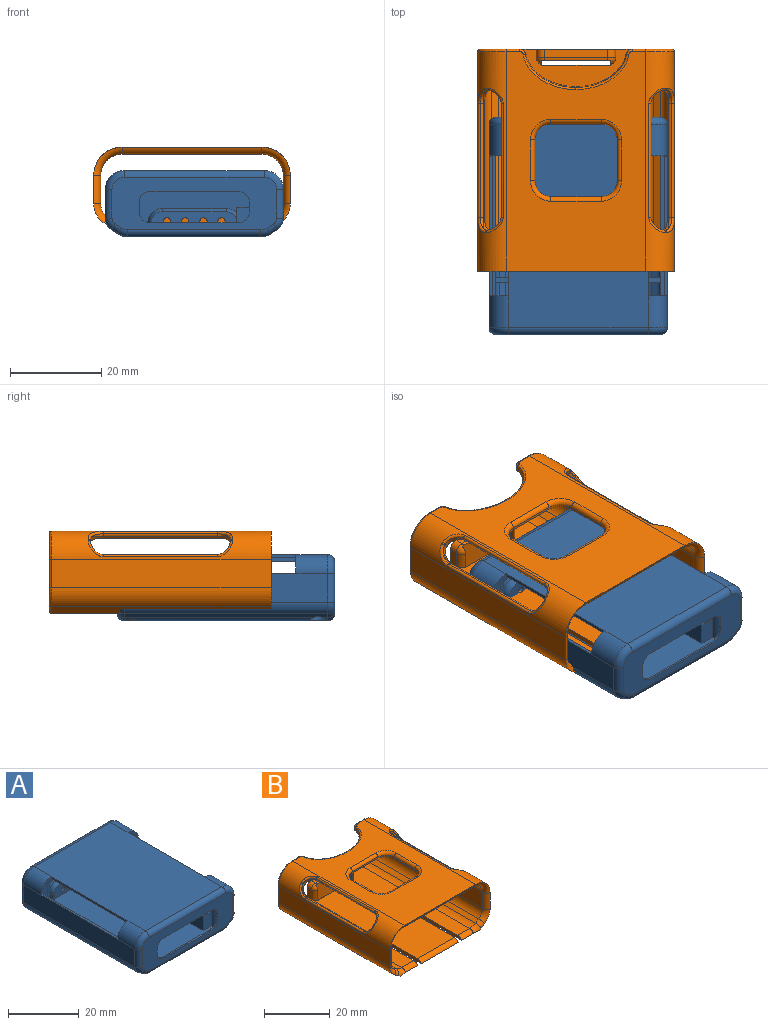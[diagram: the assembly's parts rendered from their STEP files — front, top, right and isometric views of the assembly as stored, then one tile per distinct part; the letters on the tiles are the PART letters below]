
ASSEMBLY  parts=2 mates=1
PART A: 181 faces, bbox 40.3x48.1x15.7 mm
  f0: plane 29.28x1.41mm, normal (-0.55,0,0.84), area 49.5mm2, adj f1,f15,f31,f117,f175
  f1: cylinder r=2.5mm len=29.28mm, axis (0,1,0), area 19.4mm2, adj f0,f9,f15,f31,f117
  f2: plane 5.36x1.41mm, normal (0.55,0,0.84), area 9.1mm2, adj f3,f17,f113,f178
  f3: cylinder r=2.5mm len=5.42mm, axis (0,1,0), area 7.8mm2, adj f2,f9,f17,f39,f113
  f4: plane 11.52x1.2mm, normal (1,0,0), area 12.3mm2, adj f6,f7,f9,f19,f72,f73
  f5: plane 11.52x1.2mm, normal (-1,0,0), area 12.3mm2, adj f6,f7,f8,f9,f72,f73
  f6: plane 27.05x9.99mm, normal (0,1,0), area 108.2mm2, adj f4,f5,f9,f72,f74,f75,f76,f77
  f7: plane 44.69x30.71mm, normal (0,0,-1), area 1224.5mm2, adj f4,f5,f8,f15,f16,f17,f18,f19
  f8: cylinder r=2.5mm len=11.52mm, axis (0,0,-1), area 52.4mm2, adj f5,f7,f9,f23,f32,f61,f62,f63
  f9: plane 45.69x29.18mm, normal (0,0,1), area 1231.9mm2, adj f1,f3,f4,f5,f6,f8,f15,f16
  f10: plane 30.69x0.7mm, normal (0,0,1), area 21.5mm2, adj f11,f12,f21,f54
  f11: plane 4.2x4.2mm, normal (0,1,0), area 4.2mm2, adj f10,f56,f125,f141
  f12: plane 4.2x4.2mm, normal (0,-1,0), area 4.2mm2, adj f10,f56,f123,f140
  f13: plane 44.69x6.23mm, normal (-1,0,0), area 278.4mm2, adj f46,f132,f138,f139,f144,f169
  f14: plane 35.64x6.23mm, normal (1,0,0), area 169.1mm2, adj f17,f18,f64,f66,f67,f111,f112,f113
  f15: plane 11.52x3.5mm, normal (0,-1,0), area 36.1mm2, adj f0,f1,f7,f9,f16,f22,f119,f175
  f16: cylinder r=2.5mm len=11.52mm, axis (0,0,-1), area 70.8mm2, adj f7,f9,f15,f50
  f17: plane 11.46x2.92mm, normal (0,1,0), area 29.5mm2, adj f2,f3,f7,f14,f19,f39,f120,f178
  f18: plane 11.52x3.5mm, normal (0,-1,0), area 36.1mm2, adj f7,f9,f14,f20,f27,f29,f118,f177
  f19: cylinder r=2.5mm len=11.52mm, axis (0,0,-1), area 56.4mm2, adj f4,f7,f9,f17,f39
  f20: cylinder r=2.5mm len=11.52mm, axis (0,0,-1), area 70.8mm2, adj f7,f9,f18,f50
  f21: plane 44.69x6.23mm, normal (1,0,0), area 278.4mm2, adj f10,f133,f140,f141,f147,f162
  f22: plane 35.64x6.23mm, normal (-1,0,0), area 169.1mm2, adj f15,f23,f51,f52,f53,f115,f116,f117
  f23: plane 11.46x2.92mm, normal (0,1,0), area 29.5mm2, adj f7,f8,f22,f28,f30,f32,f121,f176
  f24: plane 44.8x1.53mm, normal (-0.55,0,-0.84), area 74.9mm2, adj f102,f132,f135,f136,f148,f173
  f25: plane 45.15x1.88mm, normal (0.55,0,-0.84), area 74.9mm2, adj f84,f133,f134,f137,f151,f166
  f26: plane 44.69x29.18mm, normal (0,0,-1), area 1219.4mm2, adj f84,f90,f96,f102,f130,f131,f134,f135
  f27: plane 29.28x1.41mm, normal (0.55,0,0.84), area 49.5mm2, adj f18,f29,f112,f177
  f28: plane 5.36x1.41mm, normal (-0.55,0,0.84), area 9.1mm2, adj f23,f30,f116,f176
  f29: cylinder r=2.5mm len=29.28mm, axis (0,1,0), area 42.4mm2, adj f9,f18,f27,f112
  f30: cylinder r=2.5mm len=5.42mm, axis (0,1,0), area 7.8mm2, adj f9,f23,f28,f32,f116
  f31: cylinder r=2.5mm len=25.54mm, axis (0,1,0), area 23mm2, adj f0,f1,f117
  f32: cylinder r=2.5mm len=4.99mm, axis (0,0,-1), area 7.3mm2, adj f8,f9,f23,f30
  f33: revolved ~3.2x3.2mm, area 7.9mm2, adj f34,f37,f38,f41
  f34: cylinder r=2mm len=14mm, axis (1,0,0), area 23.7mm2, adj f33,f35,f37,f42
  f35: revolved ~3.2x3.2mm, area 7.9mm2, adj f34,f36,f37,f43
  f36: cylinder r=2mm len=1.5mm, axis (0,0,-1), area 2.5mm2, adj f9,f35,f37,f44
  f37: plane 19.05x4.03mm, normal (0,-1,0), area 65.8mm2, adj f9,f33,f34,f35,f36,f38,f106,f107
  f38: cylinder r=2mm len=1.5mm, axis (0,0,-1), area 2.5mm2, adj f9,f33,f37,f40
  f39: extruded ~4.99x2.25mm, area 13.9mm2, adj f3,f9,f17,f19
  f40: plane 1.5x0.8mm, normal (-1,0,0), area 1.2mm2, adj f9,f38,f41,f50
  f41: cylinder r=3.2mm len=3.2mm, axis (0,1,0), area 4mm2, adj f33,f40,f42,f50
  f42: plane 14x0.8mm, normal (0,0,1), area 11.2mm2, adj f34,f41,f43,f50
  f43: cylinder r=3.2mm len=3.2mm, axis (0,1,0), area 4mm2, adj f35,f42,f44,f50
  f44: plane 1.5x0.8mm, normal (1,0,0), area 1.2mm2, adj f9,f36,f43,f50
  f45: plane 36.11x11.52mm, normal (0,-1,0), area 245.6mm2, adj f74,f75,f76,f77,f128,f129,f162,f163
  f46: plane 30.69x0.7mm, normal (0,0,1), area 21.5mm2, adj f13,f47,f48,f65
  f47: plane 4.2x4.2mm, normal (0,1,0), area 4.2mm2, adj f46,f55,f124,f138
  f48: plane 4.2x4.2mm, normal (0,-1,0), area 4.2mm2, adj f46,f55,f122,f139
  f49: plane 36.11x11.52mm, normal (0,1,0), area 307.5mm2, adj f142,f143,f144,f145,f146,f147,f148,f149
  f50: plane 25.96x11.52mm, normal (0,-1,0), area 207.6mm2, adj f7,f9,f16,f20,f40,f41,f42,f43
  f51: plane 5x5mm, normal (0,1,0), area 6.3mm2, adj f7,f22,f52,f54,f70,f71,f121,f125
  f52: plane 33.68x0.8mm, normal (0,0,1), area 26.9mm2, adj f22,f51,f53,f54
  f53: plane 5x5mm, normal (0,-1,0), area 6.3mm2, adj f7,f22,f52,f54,f70,f71,f119,f123
  f54: plane 33.68x1.5mm, normal (-1,0,0), area 50.5mm2, adj f10,f51,f52,f53,f123,f125
  f55: plane 30.69x0.7mm, normal (-1,0,0), area 21.5mm2, adj f47,f48,f57,f68
  f56: plane 30.69x0.7mm, normal (1,0,0), area 21.5mm2, adj f11,f12,f57,f70
  f57: plane 44.69x30.71mm, normal (0,0,1), area 1372.1mm2, adj f55,f56,f138,f139,f140,f141,f143,f165
  f58: plane 11.15x4.99mm, normal (1,0,0), area 55.6mm2, adj f9,f59,f62,f63
  f59: plane 4.99x1mm, normal (0,1,0), area 5mm2, adj f9,f58,f60,f63
  f60: plane 13.15x4.99mm, normal (-1,0,0), area 65.6mm2, adj f9,f59,f61,f63
  f61: plane 4.99x3.32mm, normal (0,-1,0), area 16.6mm2, adj f8,f9,f60,f63
  f62: plane 4.99x2.78mm, normal (0,1,0), area 13.8mm2, adj f8,f9,f58,f63
  f63: plane 13.15x3.78mm, normal (0,0,1), area 17.9mm2, adj f8,f58,f59,f60,f61,f62
  f64: plane 33.68x0.8mm, normal (0,0,1), area 26.9mm2, adj f14,f65,f66,f67
  f65: plane 33.68x1.5mm, normal (1,0,0), area 50.5mm2, adj f46,f64,f66,f67,f122,f124
  f66: plane 5x5mm, normal (0,-1,0), area 6.3mm2, adj f7,f14,f64,f65,f68,f69,f118,f122
  f67: plane 5x5mm, normal (0,1,0), area 6.3mm2, adj f7,f14,f64,f65,f68,f69,f120,f124
  f68: plane 33.68x1.5mm, normal (0,0,-1), area 50.5mm2, adj f55,f66,f67,f69,f122,f124
  f69: plane 33.68x0.8mm, normal (-1,0,0), area 26.9mm2, adj f7,f66,f67,f68
  f70: plane 33.68x1.5mm, normal (0,0,-1), area 50.5mm2, adj f51,f53,f56,f71,f123,f125
  f71: plane 33.68x0.8mm, normal (1,0,0), area 26.9mm2, adj f7,f51,f53,f70
  f72: plane 27.05x1mm, normal (0,0,-1), area 27mm2, adj f4,f5,f6,f73
  f73: plane 27.05x1.53mm, normal (0,1,0), area 41.3mm2, adj f4,f5,f7,f72
  f74: plane 19.25x0.5mm, normal (0,0,1), area 9.6mm2, adj f6,f45,f128,f129
  f75: plane 1.99x0.5mm, normal (1,0,0), area 1mm2, adj f6,f45,f128,f179
  f76: plane 19.45x0.5mm, normal (0,0,-1), area 9.7mm2, adj f6,f45,f179,f180
  f77: plane 1.99x0.5mm, normal (-1,0,0), area 1mm2, adj f6,f45,f129,f180
  f78: plane 1.5x0.5mm, normal (1,0,0), area 0.7mm2, adj f79,f127,f130,f156
  f79: plane 18.42x3.5mm, normal (0,1,0), area 53.4mm2, adj f78,f80,f81,f106,f107,f108,f109,f126
  f80: plane 1.5x0.5mm, normal (-1,0,0), area 0.7mm2, adj f79,f126,f131,f159
  f81: plane 14x1.5mm, normal (0,0,-1), area 21mm2, adj f79,f126,f127,f160
  f82: cylinder r=1.9mm len=4.97mm, axis (0,0,-1), area 59.4mm2, adj f83,f87
  f83: plane 3.8x3.8mm, normal (0,0,-1), area 11.3mm2, adj f82
  f84: cylinder r=2mm len=4.09mm, axis (0,0,-1), area 48.2mm2, adj f25,f26,f85,f134,f137
  f85: plane 4x4mm, normal (0,0,-1), area 9.4mm2, adj f84,f86
  f86: cylinder r=1mm len=2.4mm, axis (0,0,-1), area 15.1mm2, adj f85,f87
  f87: plane 3.8x3.8mm, normal (0,0,1), area 8.2mm2, adj f82,f86
  f88: cylinder r=1.9mm len=4.97mm, axis (0,0,-1), area 59.4mm2, adj f89,f93
  f89: plane 3.8x3.8mm, normal (0,0,-1), area 11.3mm2, adj f88
  f90: cylinder r=1.5mm len=4.09mm, axis (0,0,-1), area 38.5mm2, adj f26,f91,f134
  f91: plane 3x3mm, normal (0,0,-1), area 3.9mm2, adj f90,f92
  f92: cylinder r=1mm len=2.4mm, axis (0,0,-1), area 15.1mm2, adj f91,f93
  f93: plane 3.8x3.8mm, normal (0,0,1), area 8.2mm2, adj f88,f92
  f94: cylinder r=1.9mm len=4.97mm, axis (0,0,-1), area 59.4mm2, adj f95,f99
  f95: plane 3.8x3.8mm, normal (0,0,-1), area 11.3mm2, adj f94
  f96: cylinder r=1.5mm len=4.09mm, axis (0,0,-1), area 37.9mm2, adj f26,f97,f135
  f97: plane 3x3mm, normal (0,0,-1), area 3.9mm2, adj f96,f98
  f98: cylinder r=1mm len=2.4mm, axis (0,0,-1), area 15.1mm2, adj f97,f99
  f99: plane 3.8x3.8mm, normal (0,0,1), area 8.2mm2, adj f94,f98
  f100: cylinder r=1.9mm len=4.97mm, axis (0,0,-1), area 59.4mm2, adj f101,f105
  f101: plane 3.8x3.8mm, normal (0,0,-1), area 11.3mm2, adj f100
  f102: cylinder r=2mm len=4.09mm, axis (0,0,-1), area 47.9mm2, adj f24,f26,f103,f135,f136
  f103: plane 4x4mm, normal (0,0,-1), area 9.4mm2, adj f102,f104
  f104: cylinder r=1mm len=2.4mm, axis (0,0,-1), area 15.1mm2, adj f103,f105
  f105: plane 3.8x3.8mm, normal (0,0,1), area 8.2mm2, adj f100,f104
  f106: cylinder r=0.8mm len=1.6mm, axis (0,-1,0), area 4mm2, adj f37,f79
  f107: cylinder r=0.8mm len=1.6mm, axis (0,-1,0), area 4mm2, adj f37,f79
  f108: cylinder r=0.8mm len=1.6mm, axis (0,-1,0), area 4mm2, adj f37,f79
  f109: cylinder r=0.8mm len=1.6mm, axis (0,-1,0), area 4mm2, adj f37,f79
  f110: plane 4.99x1mm, normal (1,0,0), area 5mm2, adj f9,f111,f112,f113
  f111: plane 4.53x1mm, normal (0,0,1), area 4.5mm2, adj f14,f110,f112,f113
  f112: plane 4.99x4.53mm, normal (0,1,0), area 20mm2, adj f9,f14,f27,f29,f110,f111,f177
  f113: plane 4.99x4.53mm, normal (0,-1,0), area 20mm2, adj f2,f3,f9,f14,f110,f111,f178
  f114: plane 4.99x1mm, normal (-1,0,0), area 5mm2, adj f9,f115,f116,f117
  f115: plane 4.53x1mm, normal (0,0,1), area 4.5mm2, adj f22,f114,f116,f117
  f116: plane 4.99x4.53mm, normal (0,-1,0), area 20mm2, adj f9,f22,f28,f30,f114,f115,f176
  f117: plane 4.99x4.53mm, normal (0,1,0), area 20mm2, adj f0,f1,f9,f22,f31,f114,f115,f175
  f118: cylinder r=2.7mm len=2.7mm, axis (0,1,0), area 4.5mm2, adj f7,f14,f18,f66
  f119: cylinder r=2.7mm len=2.7mm, axis (0,-1,0), area 4.5mm2, adj f7,f15,f22,f53
  f120: cylinder r=2.7mm len=2.7mm, axis (0,1,0), area 3.8mm2, adj f7,f14,f17,f67
  f121: cylinder r=2.7mm len=2.7mm, axis (0,-1,0), area 3.8mm2, adj f7,f22,f23,f51
  f122: cylinder r=3.5mm len=3.5mm, axis (0,1,0), area 8.2mm2, adj f48,f65,f66,f68
  f123: cylinder r=3.5mm len=3.5mm, axis (0,1,0), area 8.2mm2, adj f12,f53,f54,f70
  f124: cylinder r=3.5mm len=3.5mm, axis (0,1,0), area 8.2mm2, adj f47,f65,f67,f68
  f125: cylinder r=3.5mm len=3.5mm, axis (0,1,0), area 8.2mm2, adj f11,f51,f54,f70
  f126: cylinder r=2mm len=2mm, axis (0,-1,0), area 4.7mm2, adj f79,f80,f81,f161
  f127: cylinder r=2mm len=2mm, axis (0,1,0), area 4.7mm2, adj f78,f79,f81,f158
  f128: cylinder r=2.5mm len=2.5mm, axis (0,1,0), area 2mm2, adj f6,f45,f74,f75
  f129: cylinder r=2.5mm len=2.5mm, axis (0,1,0), area 2mm2, adj f6,f45,f74,f77
  f130: cylinder r=2.5mm len=3mm, axis (0,-1,0), area 8.1mm2, adj f26,f78,f79,f154,f174
  f131: cylinder r=2.5mm len=3mm, axis (0,1,0), area 8.1mm2, adj f26,f79,f80,f157,f174
  f132: cylinder r=3mm len=44.69mm, axis (0,-1,0), area 132.9mm2, adj f13,f24,f146,f171
  f133: cylinder r=3mm len=44.69mm, axis (0,1,0), area 132.9mm2, adj f21,f25,f149,f164
  f134: cylinder r=4mm len=41.44mm, axis (0,-1,0), area 91mm2, adj f25,f26,f84,f90,f153
  f135: cylinder r=4mm len=41.44mm, axis (0,-1,0), area 91mm2, adj f24,f26,f96,f102,f150
  f136: cylinder r=4mm len=2.19mm, axis (0,-1,0), area 0.7mm2, adj f24,f26,f102,f172
  f137: cylinder r=4mm len=2.19mm, axis (0,-1,0), area 0.7mm2, adj f25,f26,f84,f168
  f138: cylinder r=4.2mm len=7mm, axis (0,-1,0), area 46.2mm2, adj f13,f47,f57,f167
  f139: cylinder r=4.2mm len=7mm, axis (0,-1,0), area 46.2mm2, adj f13,f48,f57,f142
  f140: cylinder r=4.2mm len=7mm, axis (0,1,0), area 46.2mm2, adj f12,f21,f57,f145
  f141: cylinder r=4.2mm len=7mm, axis (0,1,0), area 46.2mm2, adj f11,f21,f57,f163
  f142: torus R=2.7mm, axis (0,-1,0), area 13.5mm2, adj f49,f139,f143,f144
  f143: cylinder r=1.5mm len=30.71mm, axis (1,0,0), area 72.3mm2, adj f49,f57,f142,f145
  f144: cylinder r=1.5mm len=6.23mm, axis (0,0,-1), area 14.7mm2, adj f13,f49,f142,f146
  f145: torus R=2.7mm, axis (0,-1,0), area 13.5mm2, adj f49,f140,f143,f147
  f146: torus R=1.5mm, axis (0,-1,0), area 5.7mm2, adj f49,f132,f144,f148
  f147: cylinder r=1.5mm len=6.23mm, axis (0,0,1), area 14.7mm2, adj f21,f49,f145,f149
  f148: cylinder r=1.5mm len=2.24mm, axis (0.84,0,-0.55), area 4mm2, adj f24,f49,f146,f150
  f149: torus R=1.5mm, axis (0,-1,0), area 5.7mm2, adj f49,f133,f147,f151
  f150: torus R=2.5mm, axis (0,-1,0), area 4.7mm2, adj f49,f135,f148,f152
  f151: cylinder r=1.5mm len=2.24mm, axis (0.84,0,0.55), area 4mm2, adj f25,f49,f149,f153
  f152: cylinder r=1.5mm len=3.09mm, axis (1,0,0), area 7.3mm2, adj f26,f49,f150,f154
  f153: torus R=2.5mm, axis (0,-1,0), area 4.7mm2, adj f49,f134,f151,f155
  f154: torus R=1mm, axis (0,-1,0), area 7.2mm2, adj f49,f130,f152,f156
  f155: cylinder r=1.5mm len=3.09mm, axis (1,0,0), area 7.3mm2, adj f26,f49,f153,f157
  f156: cylinder r=1.5mm len=1.5mm, axis (0,0,-1), area 1.2mm2, adj f49,f78,f154,f158
  f157: torus R=1mm, axis (0,-1,0), area 7.2mm2, adj f49,f131,f155,f159
  f158: torus R=3.5mm, axis (0,-1,0), area 9.4mm2, adj f49,f127,f156,f160
  f159: cylinder r=1.5mm len=1.5mm, axis (0,0,-1), area 1.2mm2, adj f49,f80,f157,f161
  f160: cylinder r=1.5mm len=14mm, axis (-1,0,0), area 33mm2, adj f49,f81,f158,f161
  f161: torus R=3.5mm, axis (0,-1,0), area 9.4mm2, adj f49,f126,f159,f160
  f162: cylinder r=1.5mm len=6.23mm, axis (0,0,-1), area 14.7mm2, adj f21,f45,f163,f164
  f163: torus R=2.7mm, axis (0,1,0), area 13.5mm2, adj f45,f141,f162,f165
  f164: torus R=1.5mm, axis (0,1,0), area 5.7mm2, adj f45,f133,f162,f166
  f165: cylinder r=1.5mm len=30.71mm, axis (-1,0,0), area 72.3mm2, adj f45,f57,f163,f167
  f166: cylinder r=1.5mm len=2.24mm, axis (-0.84,0,-0.55), area 4mm2, adj f25,f45,f164,f168
  f167: torus R=2.7mm, axis (0,1,0), area 13.5mm2, adj f45,f138,f165,f169
  f168: torus R=2.5mm, axis (0,1,0), area 4.7mm2, adj f45,f137,f166,f170
  f169: cylinder r=1.5mm len=6.23mm, axis (0,0,1), area 14.7mm2, adj f13,f45,f167,f171
  f170: cylinder r=1.5mm len=29.18mm, axis (-1,0,0), area 68.8mm2, adj f26,f45,f168,f172
  f171: torus R=1.5mm, axis (0,1,0), area 5.7mm2, adj f45,f132,f169,f173
  f172: torus R=2.5mm, axis (0,1,0), area 4.7mm2, adj f45,f136,f170,f173
  f173: cylinder r=1.5mm len=2.24mm, axis (-0.84,0,0.55), area 4mm2, adj f24,f45,f171,f172
  f174: cylinder r=1.5mm len=23mm, axis (1,0,0), area 48.8mm2, adj f26,f79,f130,f131
  f175: cylinder r=1.5mm len=29.28mm, axis (0,1,0), area 43.5mm2, adj f0,f15,f22,f117
  f176: cylinder r=1.5mm len=5.36mm, axis (0,1,0), area 8mm2, adj f22,f23,f28,f116
  f177: cylinder r=1.5mm len=29.28mm, axis (0,-1,0), area 43.5mm2, adj f14,f18,f27,f112
  f178: cylinder r=1.5mm len=5.36mm, axis (0,-1,0), area 8mm2, adj f2,f14,f17,f113
  f179: cylinder r=2.4mm len=2.4mm, axis (0,1,0), area 1.9mm2, adj f6,f45,f75,f76
  f180: cylinder r=2.4mm len=2.4mm, axis (0,1,0), area 1.9mm2, adj f6,f45,f76,f77
PART B: 150 faces, bbox 45.4x49.2x20.8 mm
  f0: bspline ~1.27x1.1mm, area 1.1mm2, adj f22,f27,f45,f79
  f1: bspline ~1.27x1.19mm, area 1mm2, adj f25,f26,f78,f79
  f2: cylinder r=0.5mm len=25.09mm, axis (0,1,0), area 19.2mm2, adj f3,f7,f9,f44
  f3: bspline ~4.08x3.93mm, area 4mm2, adj f2,f8,f15,f44
  f4: bspline ~3.62x3.3mm, area 4mm2, adj f5,f14,f15,f44
  f5: cylinder r=0.5mm len=25.09mm, axis (0,-1,0), area 19.2mm2, adj f4,f6,f13,f44
  f6: bspline ~4.15x3.97mm, area 4mm2, adj f5,f11,f12,f44
  f7: bspline ~3.62x3.3mm, area 4mm2, adj f2,f10,f11,f44
  f8: bspline ~3.98x3.5mm, area 1.5mm2, adj f3,f9,f47
  f9: cylinder r=1mm len=25.09mm, axis (0,1,0), area 18.2mm2, adj f2,f8,f10,f48
  f10: bspline ~3.97x3.47mm, area 1.5mm2, adj f7,f9,f49
  f11: torus R=5.7mm, axis (0,1,0), area 0.3mm2, adj f6,f7,f44,f50
  f12: bspline ~3.53x2.95mm, area 1.5mm2, adj f6,f13,f51
  f13: cylinder r=1mm len=25.09mm, axis (0,1,0), area 18.2mm2, adj f5,f12,f14,f52
  f14: bspline ~3.97x3.47mm, area 1.5mm2, adj f4,f13,f53
  f15: torus R=5.7mm, axis (0,-1,0), area 0.3mm2, adj f3,f4,f44,f54
  f16: bspline ~3.97x3.47mm, area 1.5mm2, adj f17,f42,f58
  f17: cylinder r=1mm len=25.09mm, axis (0,1,0), area 18.2mm2, adj f16,f18,f41,f59
  f18: bspline ~3.97x3.47mm, area 1.5mm2, adj f17,f40,f60
  f19: bspline ~3.97x3.47mm, area 1.5mm2, adj f20,f38,f62
  f20: cylinder r=1mm len=25.09mm, axis (0,1,0), area 18.2mm2, adj f19,f21,f37,f63
  f21: bspline ~3.53x2.95mm, area 1.5mm2, adj f20,f36,f64
  f22: bspline ~1.76x1.51mm, area 0.6mm2, adj f0,f23,f66,f89
  f23: bspline ~11.81x7.8mm, area 11.1mm2, adj f22,f24,f27,f67
  f24: bspline ~11.78x7.8mm, area 11.1mm2, adj f23,f25,f26,f68
  f25: bspline ~1.48x1.47mm, area 0.6mm2, adj f1,f24,f69,f99
  f26: bspline ~11.66x7.94mm, area 7.7mm2, adj f1,f24,f27,f79
  f27: bspline ~11.66x7.94mm, area 7.7mm2, adj f0,f23,f26,f79
  f28: torus R=4.5mm, axis (0,0,-1), area 9.5mm2, adj f29,f35,f72,f79
  f29: cylinder r=1mm len=8.97mm, axis (0,-1,0), area 14.1mm2, adj f28,f30,f71,f79
  f30: torus R=4.5mm, axis (0,0,-1), area 9.5mm2, adj f29,f31,f70,f79
  f31: cylinder r=1mm len=11mm, axis (1,0,0), area 17.3mm2, adj f30,f32,f77,f79
  f32: torus R=4.5mm, axis (0,0,-1), area 9.5mm2, adj f31,f33,f76,f79
  f33: cylinder r=1mm len=8.97mm, axis (0,-1,0), area 14.1mm2, adj f32,f34,f75,f79
  f34: torus R=4.5mm, axis (0,0,-1), area 9.5mm2, adj f33,f35,f74,f79
  f35: cylinder r=1mm len=11mm, axis (1,0,0), area 17.3mm2, adj f28,f34,f73,f79
  f36: bspline ~3.62x3.3mm, area 4mm2, adj f21,f37,f43,f80
  f37: cylinder r=0.5mm len=25.09mm, axis (0,1,0), area 19.2mm2, adj f20,f36,f38,f80
  f38: bspline ~3.62x3.3mm, area 4mm2, adj f19,f37,f39,f80
  f39: torus R=5.7mm, axis (0,-1,0), area 0.3mm2, adj f38,f40,f61,f80
  f40: bspline ~3.75x3.41mm, area 4mm2, adj f18,f39,f41,f80
  f41: cylinder r=0.5mm len=25.09mm, axis (0,-1,0), area 19.2mm2, adj f17,f40,f42,f80
  f42: bspline ~3.62x3.3mm, area 4mm2, adj f16,f41,f43,f80
  f43: torus R=5.7mm, axis (0,1,0), area 0.3mm2, adj f36,f42,f57,f80
  f44: cylinder r=6.2mm len=48.14mm, axis (0,1,0), area 213.4mm2, adj f2,f3,f4,f5,f6,f7,f11,f15
  f45: cylinder r=0.5mm len=0.5mm, axis (1,0,0), area 0.1mm2, adj f0,f79,f88,f89
  f46: torus R=6.6mm, axis (0,1,0), area 21.2mm2, adj f44,f55,f65,f90
  f47: cylinder r=2.8mm len=3.43mm, axis (0.71,0,-0.71), area 3.2mm2, adj f8,f48,f54,f90
  f48: plane 25.09x0.32mm, normal (0.71,0,0.71), area 11.2mm2, adj f9,f47,f49,f90
  f49: cylinder r=2.8mm len=3.43mm, axis (0.71,0,-0.71), area 3.2mm2, adj f10,f48,f50,f90
  f50: plane 0.95x0.95mm, normal (0,1,0), area 0.3mm2, adj f11,f49,f51,f90
  f51: cylinder r=2.8mm len=3.43mm, axis (0.71,0,-0.71), area 3.2mm2, adj f12,f50,f52,f90
  f52: plane 25.09x0.32mm, normal (-0.71,0,-0.71), area 11.2mm2, adj f13,f51,f53,f90
  f53: cylinder r=2.8mm len=3.43mm, axis (0.71,0,-0.71), area 3.2mm2, adj f14,f52,f54,f90
  f54: plane 0.95x0.95mm, normal (0,-1,0), area 0.3mm2, adj f15,f47,f53,f90
  f55: cylinder r=1.9mm len=6.23mm, axis (0,0,-1), area 16.1mm2, adj f46,f83,f84,f91
  f56: torus R=6.6mm, axis (0,-1,0), area 21.2mm2, adj f65,f80,f81,f97
  f57: plane 0.95x0.95mm, normal (0,1,0), area 0.3mm2, adj f43,f58,f64,f97
  f58: cylinder r=2.8mm len=3.43mm, axis (-0.71,0,-0.71), area 3.2mm2, adj f16,f57,f59,f97
  f59: plane 25.09x0.32mm, normal (-0.71,0,0.71), area 11.2mm2, adj f17,f58,f60,f97
  f60: cylinder r=2.8mm len=3.43mm, axis (-0.71,0,-0.71), area 3.2mm2, adj f18,f59,f61,f97
  f61: plane 0.95x0.95mm, normal (0,-1,0), area 0.3mm2, adj f39,f60,f62,f97
  f62: cylinder r=2.8mm len=3.43mm, axis (-0.71,0,-0.71), area 3.2mm2, adj f19,f61,f63,f97
  f63: plane 25.09x0.32mm, normal (0.71,0,-0.71), area 11.2mm2, adj f20,f62,f64,f97
  f64: cylinder r=2.8mm len=3.43mm, axis (-0.71,0,-0.71), area 3.2mm2, adj f21,f57,f63,f97
  f65: cylinder r=1.9mm len=30.71mm, axis (-1,0,0), area 79.3mm2, adj f46,f56,f79,f98
  f66: cylinder r=1.5mm len=1.47mm, axis (0,0,-1), area 1.5mm2, adj f22,f67,f98,f120
  f67: extruded ~10.93x7mm, area 7mm2, adj f23,f66,f68,f98
  f68: extruded ~10.93x7mm, area 7mm2, adj f24,f67,f69,f98
  f69: cylinder r=1.5mm len=1.47mm, axis (0,0,-1), area 1.5mm2, adj f25,f68,f98,f120
  f70: cylinder r=3.5mm len=3.5mm, axis (0,0,-1), area 2.7mm2, adj f30,f71,f77,f98
  f71: plane 8.97x0.5mm, normal (1,0,0), area 4.5mm2, adj f29,f70,f72,f98
  f72: cylinder r=3.5mm len=3.5mm, axis (0,0,-1), area 2.7mm2, adj f28,f71,f73,f98
  f73: plane 11x0.5mm, normal (0,1,0), area 5.5mm2, adj f35,f72,f74,f98
  f74: cylinder r=3.5mm len=3.5mm, axis (0,0,-1), area 2.7mm2, adj f34,f73,f75,f98
  f75: plane 8.97x0.5mm, normal (-1,0,0), area 4.5mm2, adj f33,f74,f76,f98
  f76: cylinder r=3.5mm len=3.5mm, axis (0,0,-1), area 2.7mm2, adj f32,f75,f77,f98
  f77: plane 11x0.5mm, normal (0,-1,0), area 5.5mm2, adj f31,f70,f76,f98
  f78: cylinder r=0.5mm len=0.5mm, axis (-1,0,0), area 0.1mm2, adj f1,f79,f99,f100
  f79: plane 48.18x30.74mm, normal (0,0,1), area 985.4mm2, adj f0,f1,f26,f27,f28,f29,f30,f31
  f80: cylinder r=6.2mm len=48.14mm, axis (0,1,0), area 213.4mm2, adj f36,f37,f38,f39,f40,f41,f42,f43
  f81: cylinder r=1.9mm len=6.23mm, axis (0,0,-1), area 16.1mm2, adj f56,f96,f104,f105
  f82: plane 46.79x1.41mm, normal (0.55,0,0.84), area 79.1mm2, adj f92,f114,f115,f120
  f83: plane 48.14x6.23mm, normal (-1,0,0), area 300mm2, adj f44,f55,f86,f116
  f84: torus R=5.4mm, axis (0,1,0), area 10.3mm2, adj f55,f92,f114,f116
  f85: torus R=4.5mm, axis (0,-1,0), area 3.8mm2, adj f86,f116,f117,f120
  f86: cylinder r=0.5mm len=6.23mm, axis (0,0,-1), area 4.9mm2, adj f83,f85,f87,f120
  f87: torus R=5.7mm, axis (0,-1,0), area 7.4mm2, adj f44,f86,f88,f120
  f88: cylinder r=0.5mm len=2.87mm, axis (-1,0,0), area 2.3mm2, adj f45,f79,f87,f120
  f89: cylinder r=1.34mm len=0.09mm, axis (0.99,0,-0.11), area 0mm2, adj f22,f45,f120
  f90: cylinder r=4.7mm len=46.79mm, axis (0,1,0), area 156mm2, adj f46,f47,f48,f49,f50,f51,f52,f53
  f91: plane 46.79x6.23mm, normal (1,0,0), area 291.5mm2, adj f55,f90,f92,f120
  f92: cylinder r=3.5mm len=46.79mm, axis (0,1,0), area 162.3mm2, adj f82,f84,f91,f120
  f93: cylinder r=1.69mm len=1.81mm, axis (0,-1,0), area 4.8mm2, adj f108,f109,f110,f120
  f94: cylinder r=1.69mm len=1.81mm, axis (0,-1,0), area 4.8mm2, adj f107,f109,f113,f120
  f95: cylinder r=3.5mm len=46.79mm, axis (0,1,0), area 162.3mm2, adj f96,f105,f106,f120
  f96: plane 46.79x6.23mm, normal (-1,0,0), area 291.5mm2, adj f81,f95,f97,f120
  f97: cylinder r=4.7mm len=46.79mm, axis (0,1,0), area 156mm2, adj f56,f57,f58,f59,f60,f61,f62,f63
  f98: plane 47.19x31.11mm, normal (0,0,-1), area 1016.5mm2, adj f65,f66,f67,f68,f69,f70,f71,f72
  f99: cylinder r=1.33mm len=0.09mm, axis (0.99,0,0.11), area 0mm2, adj f25,f78,f120
  f100: cylinder r=0.5mm len=2.87mm, axis (1,0,0), area 2.3mm2, adj f78,f79,f101,f120
  f101: torus R=5.7mm, axis (0,-1,0), area 7.4mm2, adj f80,f100,f102,f120
  f102: cylinder r=0.5mm len=6.23mm, axis (0,0,-1), area 4.9mm2, adj f101,f103,f104,f120
  f103: torus R=4.5mm, axis (0,1,0), area 3.8mm2, adj f102,f120,f123,f124
  f104: plane 48.14x6.23mm, normal (1,0,0), area 300mm2, adj f80,f81,f102,f124
  f105: torus R=5.4mm, axis (0,-1,0), area 10.3mm2, adj f81,f95,f124,f125
  f106: plane 46.79x1.41mm, normal (-0.55,0,0.84), area 79.1mm2, adj f95,f120,f125,f126
  f107: plane 3.61x1.81mm, normal (1,0,0), area 6.5mm2, adj f94,f112,f120,f127
  f108: plane 3.61x1.81mm, normal (-1,0,0), area 6.5mm2, adj f93,f111,f120,f127
  f109: plane 14.02x1.81mm, normal (0,0,1), area 25.4mm2, adj f93,f94,f120,f128
  f110: sphere r=1.69mm, area 3.4mm2, adj f93,f111,f128,f129,f148
  f111: cylinder r=1.69mm len=3.61mm, axis (0,0,-1), area 7.8mm2, adj f108,f110,f127,f129
  f112: cylinder r=1.69mm len=3.61mm, axis (0,0,-1), area 7.8mm2, adj f107,f113,f127,f130
  f113: sphere r=1.69mm, area 3.5mm2, adj f94,f112,f128,f130,f148
  f114: cylinder r=1.9mm len=2.24mm, axis (0.84,0,-0.55), area 4.4mm2, adj f82,f84,f137,f138
  f115: cylinder r=4.5mm len=46.79mm, axis (0,1,0), area 122mm2, adj f82,f120,f127,f137
  f116: cylinder r=5mm len=48.14mm, axis (0,1,0), area 238.6mm2, adj f83,f84,f85,f138
  f117: cylinder r=0.5mm len=1.69mm, axis (0.84,0,-0.55), area 1.3mm2, adj f85,f118,f120,f138
  f118: bspline ~1.07x1.03mm, area 0.7mm2, adj f117,f119,f138,f139
  f119: torus R=5.5mm, axis (0,-1,0), area 0mm2, adj f118,f120,f139
  f120: plane 42.11x17.02mm, normal (0,1,0), area 155.9mm2, adj f66,f69,f82,f85,f86,f87,f88,f89
  f121: torus R=5.5mm, axis (0,1,0), area 0mm2, adj f120,f122,f141
  f122: bspline ~1.07x1.03mm, area 0.7mm2, adj f121,f123,f141,f142
  f123: cylinder r=0.5mm len=1.69mm, axis (-0.84,0,-0.55), area 1.3mm2, adj f103,f120,f122,f142
  f124: cylinder r=5mm len=48.14mm, axis (0,1,0), area 238.6mm2, adj f103,f104,f105,f142
  f125: cylinder r=1.9mm len=2.24mm, axis (-0.84,0,-0.55), area 4.4mm2, adj f105,f106,f142,f143
  f126: cylinder r=4.5mm len=46.79mm, axis (0,1,0), area 122mm2, adj f106,f120,f127,f143
  f127: plane 46.79x29.18mm, normal (0,0,1), area 1247.5mm2, adj f107,f108,f111,f112,f115,f120,f126,f129
  f128: cylinder r=1.69mm len=14.02mm, axis (1,0,0), area 10mm2, adj f109,f110,f113,f148
  f129: plane 6.4x1.33mm, normal (1,0,0), area 5.3mm2, adj f110,f111,f127,f147,f148,f149
  f130: plane 6.07x1mm, normal (-1,0,0), area 5.3mm2, adj f112,f113,f127,f147,f148,f149
  f131: plane 22.42x1mm, normal (1,0,0), area 21.9mm2, adj f127,f132,f146,f149
  f132: cylinder r=1.9mm len=16mm, axis (1,0,0), area 32.8mm2, adj f127,f131,f133,f149
  f133: plane 22.42x1mm, normal (-1,0,0), area 21.9mm2, adj f127,f132,f134,f149
  f134: plane 1.4x1mm, normal (0,-1,0), area 1.4mm2, adj f127,f133,f135,f149
  f135: plane 22.42x1mm, normal (1,0,0), area 21.9mm2, adj f127,f134,f136,f149
  f136: cylinder r=1.9mm len=5.19mm, axis (1,0,0), area 10.6mm2, adj f127,f135,f137,f149
  f137: torus R=6.4mm, axis (0,1,0), area 7mm2, adj f114,f115,f136,f138,f149
  f138: plane 48.37x2.36mm, normal (-0.55,0,-0.84), area 123.5mm2, adj f114,f116,f117,f118,f137,f139,f149
  f139: bspline ~0.51x0.5mm, area 0.2mm2, adj f118,f119,f138,f140,f149
  f140: cylinder r=0.5mm len=33.77mm, axis (1,0,0), area 26.5mm2, adj f120,f139,f141,f149
  f141: bspline ~0.51x0.5mm, area 0.2mm2, adj f121,f122,f140,f142,f149
  f142: plane 48.37x2.36mm, normal (0.55,0,-0.84), area 123.5mm2, adj f122,f123,f124,f125,f141,f143,f149
  f143: torus R=6.4mm, axis (0,-1,0), area 7mm2, adj f125,f126,f142,f144,f149
  f144: cylinder r=1.9mm len=5.19mm, axis (-1,0,0), area 10.6mm2, adj f127,f143,f145,f149
  f145: plane 22.42x1mm, normal (-1,0,0), area 21.9mm2, adj f127,f144,f146,f149
  f146: plane 1.4x1mm, normal (0,-1,0), area 1.4mm2, adj f127,f131,f145,f149
  f147: plane 15x1mm, normal (0,1,0), area 15mm2, adj f127,f129,f130,f149
  f148: plane 15.1x6.25mm, normal (0,-1,0), area 92.3mm2, adj f110,f113,f128,f129,f130,f149
  f149: plane 48.46x34.59mm, normal (0,0,-1), area 1567mm2, adj f129,f130,f131,f132,f133,f134,f135,f136
PLACE A t=(149.79,226.05,-84.42)mm
PLACE B t=(93.57,176.44,-81.31)mm
MATE fastened A.f21 <-> B.f96  axis (1,0,0) through (-50.24,-19.14,12.67)mm
